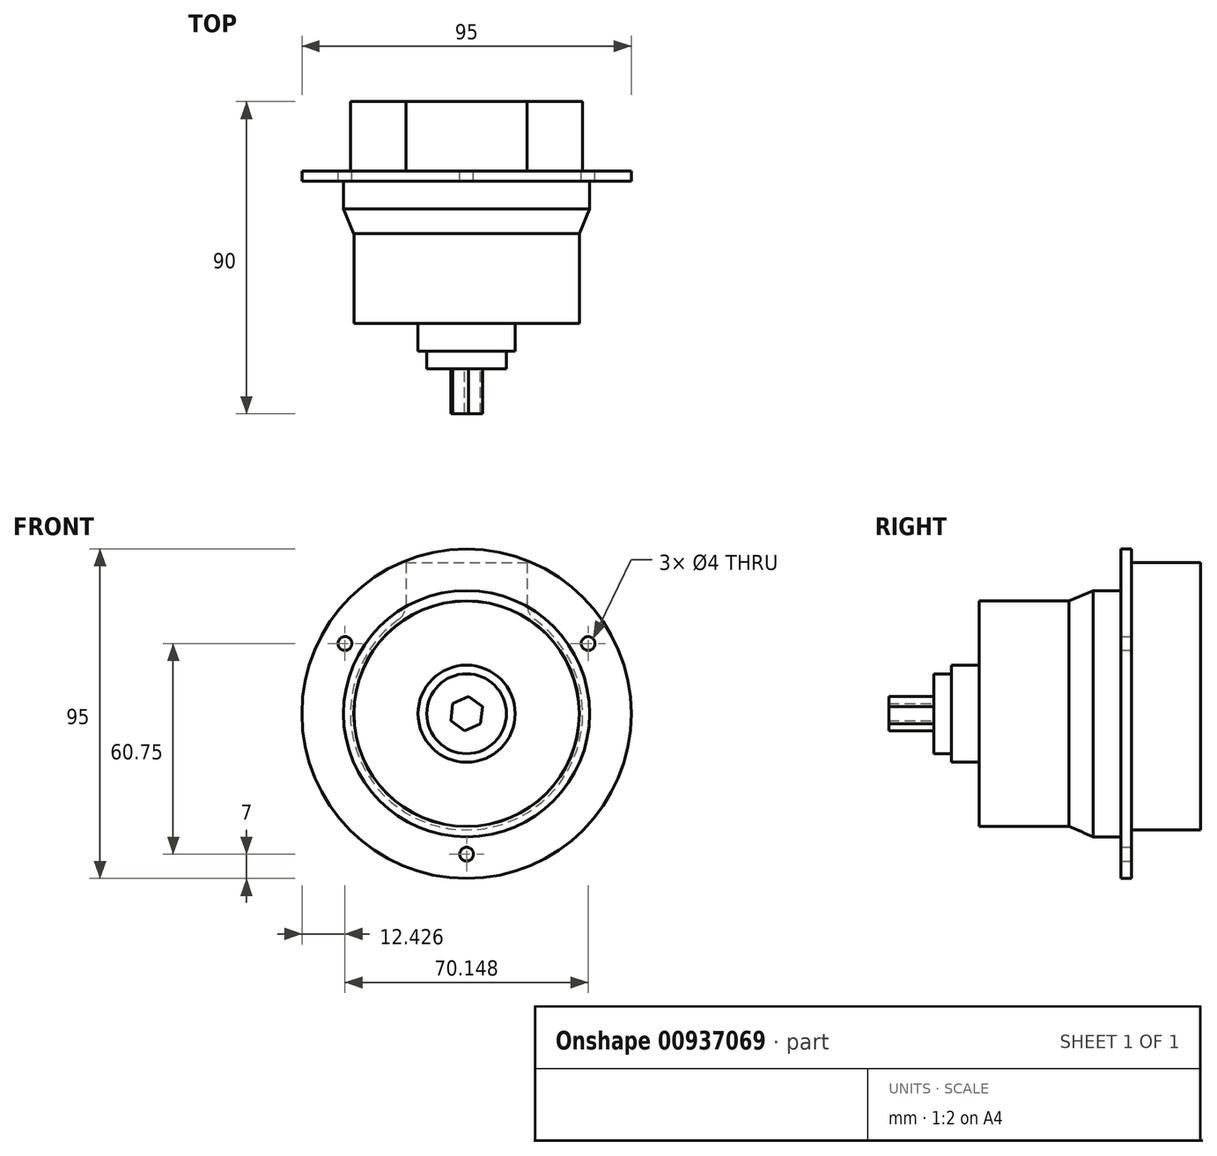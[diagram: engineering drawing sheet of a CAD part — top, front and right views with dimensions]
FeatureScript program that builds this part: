
annotation { "Feature Type Name" : "Feature", "Feature Type Description" : "" }
export const myFeature = defineFeature(function(context is Context, id is Id, definition is map)
    precondition{}
    {
        {
            var Q0;
            Q0=qCreatedBy(makeId("Front.planeOp"),FACE);
            var sketch = newSketch(context, id + "F0", { "sketchPlane" : qUnion([Q0])});
            skArc(sketch, "E0", {"start": v(-19.58, 27.18) * mm, "mid": v(0, -33.5) * mm, "end": v(19.58, 27.18) * mm});
            skLineSegment(sketch, "E1", {"start": v(0, 43.57) * mm, "end": v(17.5, 43.57) * mm});
            skLineSegment(sketch, "E2", {"start": v(17.5, 43.57) * mm, "end": v(17.5, 31.24) * mm});
            skLineSegment(sketch, "E3", {"start": v(0, 43.57) * mm, "end": v(-17.5, 43.57) * mm});
            skLineSegment(sketch, "E4", {"start": v(-17.5, 43.57) * mm, "end": v(-17.5, 31.24) * mm});
            skPoint(sketch, "E5.visualSharp", {"position": v(17.5, 28.57) * mm});
            skArc(sketch, "E5.filletArc", {"start": v(17.5, 31.24) * mm, "mid": v(18.05, 28.96) * mm, "end": v(19.58, 27.18) * mm});
            skPoint(sketch, "E6.visualSharp", {"position": v(-17.5, 28.57) * mm});
            skArc(sketch, "E6.filletArc", {"start": v(-19.58, 27.18) * mm, "mid": v(-18.05, 28.96) * mm, "end": v(-17.5, 31.24) * mm});
            skSolve(sketch);
        }
        {
            var Q0;
            Q0=makeQuery(id+"F0.imprint","IMPRINT",FACE,{"disambiguationData":[TD([[makeQuery(id+"F0.imprint","IMPRINT",EDGE,{"derivedFrom":sQuery(id+"F0.wireOp",EDGE,"E0")}),1.0]])]});
            extrude(context, id + "F1", {"entities" : qUnion([Q0]), "oppositeDirection" : true, "depth" : 20 * mm, "offsetDistance" : 25 * mm});
        }
        {
            var Q0;
            Q0=makeQuery(id+"F1.opExtrude","CAP_FACE",FACE,{"disambiguationData":[OSD([sQuery(id+"F0.wireOp",EDGE,"E0"),sQuery(id+"F0.wireOp",EDGE,"E1"),sQuery(id+"F0.wireOp",EDGE,"E2"),sQuery(id+"F0.wireOp",EDGE,"E3"),sQuery(id+"F0.wireOp",EDGE,"E4"),sQuery(id+"F0.wireOp",EDGE,"E5.filletArc"),sQuery(id+"F0.wireOp",EDGE,"E6.filletArc")])],"isStart":true});
            var sketch = newSketch(context, id + "F2", { "sketchPlane" : qUnion([Q0])});
            skCircle(sketch, "E7", {"center": v(0, 0) * mm, "radius": 47.5 * mm});
            skSolve(sketch);
        }
        {
            var Q0;
            Q0 = qSketchRegion(id + "F2", true);
            extrude(context, id + "F3", {"entities" : qUnion([Q0]), "operationType" : NewBodyOperationType.ADD, "depth" : 3 * mm, "offsetDistance" : 25 * mm});
        }
        {
            var Q0;
            Q0=makeQuery(id+"F3.opExtrude","CAP_FACE",FACE,{"disambiguationData":[OSD([sQuery(id+"F2.wireOp",EDGE,"E7")])],"isStart":false});
            var sketch = newSketch(context, id + "F4", { "sketchPlane" : qUnion([Q0])});
            skCircle(sketch, "E8", {"center": v(0, 0) * mm, "radius": 35.5 * mm});
            skSolve(sketch);
        }
        {
            var Q0;
            Q0=makeQuery(id+"F4.imprint","IMPRINT",FACE,{"disambiguationData":[TD([[makeQuery(id+"F4.imprint","IMPRINT",EDGE,{"derivedFrom":sQuery(id+"F4.wireOp",EDGE,"E8")}),1.0]])]});
            extrude(context, id + "F5", {"entities" : qUnion([Q0]), "operationType" : NewBodyOperationType.ADD, "depth" : 8 * mm, "offsetDistance" : 25 * mm});
        }
        {
            var Q0;
            Q0=makeQuery(id+"F5.opExtrude","CAP_FACE",FACE,{"disambiguationData":[OSD([sQuery(id+"F4.wireOp",EDGE,"E8")])],"isStart":false});
            var sketch = newSketch(context, id + "F6", { "sketchPlane" : qUnion([Q0])});
            skCircle(sketch, "E9", {"center": v(0, 0) * mm, "radius": 35.5 * mm});
            skSolve(sketch);
        }
        {
            var Q0;
            Q0 = qSketchRegion(id + "F6", true);
            extrude(context, id + "F7", {"entities" : qUnion([Q0]), "depth" : 7 * mm, "offsetDistance" : 25 * mm, "hasDraft" : true, "draftAngle" : 23 * degree, "draftPullDirection" : true});
        }
        {
            var Q0;
            Q0=makeQuery(id+"F7.opExtrude","CAP_FACE",FACE,{"disambiguationData":[OSD([sQuery(id+"F6.wireOp",EDGE,"E9")])],"isStart":false});
            var sketch = newSketch(context, id + "F8", { "sketchPlane" : qUnion([Q0])});
            skCircle(sketch, "E10", {"center": v(0, 0) * mm, "radius": 32.5 * mm});
            skSolve(sketch);
        }
        {
            var Q0;
            Q0 = qSketchRegion(id + "F8", true);
            extrude(context, id + "F9", {"entities" : qUnion([Q0]), "depth" : 26 * mm, "offsetDistance" : 25 * mm});
        }
        {
            var Q0;
            Q0=makeQuery(id+"F9.opExtrude","CAP_FACE",FACE,{"disambiguationData":[OSD([sQuery(id+"F8.wireOp",EDGE,"E10")])],"isStart":false});
            var sketch = newSketch(context, id + "F10", { "sketchPlane" : qUnion([Q0])});
            skCircle(sketch, "E11", {"center": v(0, 0) * mm, "radius": 14 * mm});
            skSolve(sketch);
        }
        {
            var Q0;
            Q0=makeQuery(id+"F10.imprint","IMPRINT",FACE,{"disambiguationData":[TD([[makeQuery(id+"F10.imprint","IMPRINT",EDGE,{"derivedFrom":sQuery(id+"F10.wireOp",EDGE,"E11")}),1.0]])]});
            extrude(context, id + "F11", {"entities" : qUnion([Q0]), "depth" : 8 * mm, "offsetDistance" : 25 * mm});
        }
        {
            var Q0;
            Q0=makeQuery(id+"F11.opExtrude","CAP_FACE",FACE,{"disambiguationData":[OSD([sQuery(id+"F10.wireOp",EDGE,"E11")])],"isStart":false});
            var sketch = newSketch(context, id + "F12", { "sketchPlane" : qUnion([Q0])});
            skCircle(sketch, "E12", {"center": v(0, 0) * mm, "radius": 11.5 * mm});
            skSolve(sketch);
        }
        {
            var Q0;
            Q0=makeQuery(id+"F12.imprint","IMPRINT",FACE,{"disambiguationData":[TD([[makeQuery(id+"F12.imprint","IMPRINT",EDGE,{"derivedFrom":sQuery(id+"F12.wireOp",EDGE,"E12")}),1.0]])]});
            extrude(context, id + "F13", {"entities" : qUnion([Q0]), "depth" : 5 * mm, "offsetDistance" : 25 * mm});
        }
        {
            var Q0;
            Q0=makeQuery(id+"F13.opExtrude","CAP_FACE",FACE,{"disambiguationData":[OSD([sQuery(id+"F12.wireOp",EDGE,"E12")])],"isStart":false});
            var sketch = newSketch(context, id + "F14", { "sketchPlane" : qUnion([Q0])});
            skCircle(sketch, "E13.cCircle", {"center": v(0, 0) * mm, "radius": 4.32 * mm, "construction": true});
            skLineSegment(sketch, "E13.0", {"start": v(0.56, 4.96) * mm, "end": v(4.57, 2) * mm});
            skLineSegment(sketch, "E13.1", {"start": v(4.57, 2) * mm, "end": v(4.02, -2.96) * mm});
            skLineSegment(sketch, "E13.2", {"start": v(4.02, -2.96) * mm, "end": v(-0.56, -4.96) * mm});
            skLineSegment(sketch, "E13.3", {"start": v(-0.56, -4.96) * mm, "end": v(-4.57, -2) * mm});
            skLineSegment(sketch, "E13.4", {"start": v(-4.57, -2) * mm, "end": v(-4.02, 2.96) * mm});
            skLineSegment(sketch, "E13.5", {"start": v(-4.02, 2.96) * mm, "end": v(0.56, 4.96) * mm});
            skPoint(sketch, "E13.0.midPoint", {"position": v(2.57, 3.48) * mm});
            skSolve(sketch);
        }
        {
            var Q0;
            Q0=makeQuery(id+"F14.imprint","IMPRINT",FACE,{"disambiguationData":[TD([[makeQuery(id+"F14.imprint","IMPRINT",EDGE,{"derivedFrom":sQuery(id+"F14.wireOp",EDGE,"E13.0")}),-1.0]])]});
            extrude(context, id + "F15", {"entities" : qUnion([Q0]), "operationType" : NewBodyOperationType.ADD, "depth" : 13 * mm, "offsetDistance" : 25 * mm});
        }
        {
            var Q0;
            Q0=makeQuery(id+"F3.opExtrude","CAP_FACE",FACE,{"disambiguationData":[OSD([sQuery(id+"F2.wireOp",EDGE,"E7")])],"isStart":true});
            var sketch = newSketch(context, id + "F16", { "sketchPlane" : qUnion([Q0])});
            skLineSegment(sketch, "E14", {"start": v(0, 0) * mm, "end": v(0, -47.5) * mm, "construction": true});
            skPoint(sketch, "E14.endSnap0", {"position": v(0, -33.5) * mm});
            skCircle(sketch, "E15", {"center": v(0, -40.5) * mm, "radius": 2 * mm});
            skLineSegment(sketch, "E16", {"start": v(0, 0) * mm, "end": v(-41.14, 23.75) * mm, "construction": true});
            skLineSegment(sketch, "E17", {"start": v(0, 0) * mm, "end": v(41.14, 23.75) * mm, "construction": true});
            skCircle(sketch, "E18", {"center": v(-35.07, 20.25) * mm, "radius": 2 * mm});
            skCircle(sketch, "E19", {"center": v(35.07, 20.25) * mm, "radius": 2 * mm});
            skLineSegment(sketch, "E20", {"start": v(47.5, 0) * mm, "end": v(0, 0) * mm, "construction": true});
            skLineSegment(sketch, "E21", {"start": v(-47.5, 0) * mm, "end": v(0, 0) * mm, "construction": true});
            skLineSegment(sketch, "E22", {"start": v(41.14, 23.75) * mm, "end": v(41.14, 0) * mm, "construction": true});
            skSolve(sketch);
        }
        {
            var Q0;
            Q0 = qSketchRegion(id + "F16", true);
            extrude(context, id + "F17", {"entities" : qUnion([Q0]), "operationType" : NewBodyOperationType.REMOVE, "endBound" : BoundingType.THROUGH_ALL, "oppositeDirection" : true, "depth" : 25 * mm, "offsetDistance" : 25 * mm});
        }
    });
